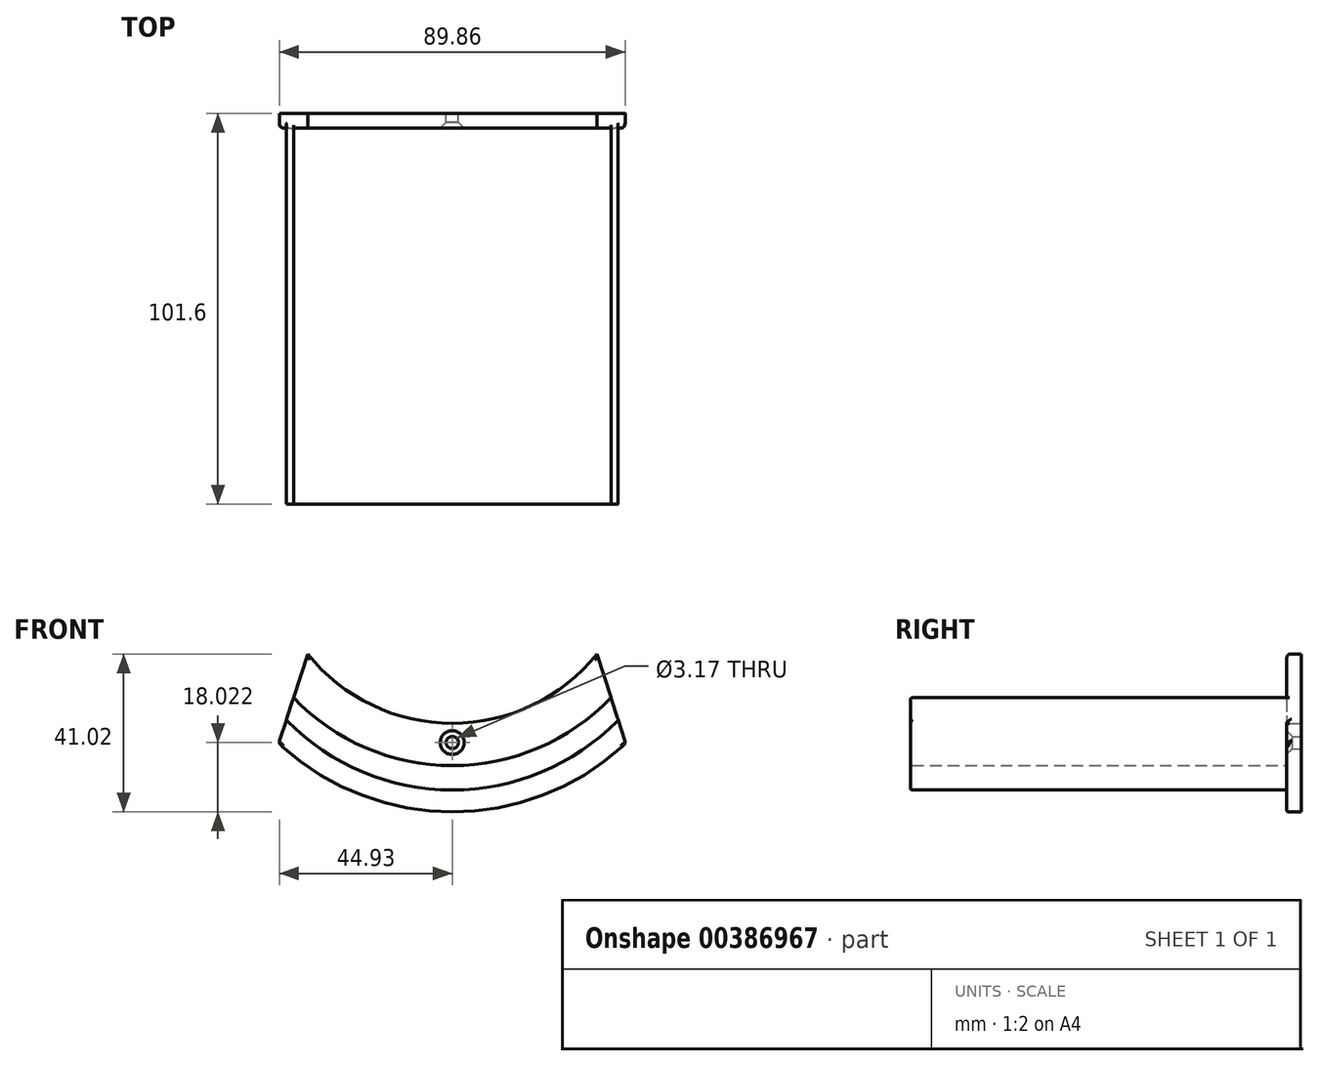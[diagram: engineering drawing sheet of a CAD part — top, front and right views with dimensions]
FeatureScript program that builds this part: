
annotation { "Feature Type Name" : "Feature", "Feature Type Description" : "" }
export const myFeature = defineFeature(function(context is Context, id is Id, definition is map)
    precondition{}
    {
        {
            var Q0;
            Q0=qCreatedBy(makeId("Front.planeOp"),FACE);
            var sketch = newSketch(context, id + "F0", { "sketchPlane" : qUnion([Q0])});
            skArc(sketch, "E0", {"start": v(-43.16, 1.57) * mm, "mid": v(0, -16.6) * mm, "end": v(43.16, 1.57) * mm});
            skArc(sketch, "E1", {"start": v(-41.28, 7.37) * mm, "mid": v(0, -10.26) * mm, "end": v(41.28, 7.37) * mm});
            skLineSegment(sketch, "E2", {"start": v(-43.16, 1.57) * mm, "end": v(-41.28, 7.37) * mm});
            skArc(sketch, "E3", {"start": v(-45.12, -4.47) * mm, "mid": v(0, -22.3) * mm, "end": v(45.12, -4.47) * mm});
            skLineSegment(sketch, "E4", {"start": v(-45.12, -4.47) * mm, "end": v(-43.16, 1.57) * mm});
            skLineSegment(sketch, "E5", {"start": v(45.12, -4.47) * mm, "end": v(43.16, 1.57) * mm});
            skPoint(sketch, "E6", {"position": v(0, -10.26) * mm});
            skPoint(sketch, "E7", {"position": v(0, -16.6) * mm});
            skLineSegment(sketch, "E8", {"start": v(43.16, 1.57) * mm, "end": v(41.28, 7.37) * mm});
            skCircle(sketch, "E9", {"center": v(0, -4.27) * mm, "radius": 1.59 * mm});
            skLineSegment(sketch, "E10", {"start": v(-41.28, 7.37) * mm, "end": v(-37.6, 18.73) * mm});
            skLineSegment(sketch, "E11", {"start": v(41.28, 7.37) * mm, "end": v(37.6, 18.73) * mm});
            skArc(sketch, "E12", {"start": v(-37.6, 18.73) * mm, "mid": v(0, 0.72) * mm, "end": v(37.6, 18.73) * mm});
            skSolve(sketch);
        }
        {
            var Q0;
            Q0=makeQuery(id+"F0.imprint","IMPRINT",FACE,{"disambiguationData":[TD([[makeQuery(id+"F0.imprint","IMPRINT",EDGE,{"derivedFrom":sQuery(id+"F0.wireOp",EDGE,"E0")}),1.0]])]});
            extrude(context, id + "F1", {"entities" : qUnion([Q0]), "depth" : 101.6 * mm, "offsetDistance" : 25.4 * mm});
        }
        {
            var Q0;
            Q0=makeQuery(id+"F0.imprint","IMPRINT",FACE,{"disambiguationData":[TD([[makeQuery(id+"F0.imprint","IMPRINT",EDGE,{"derivedFrom":sQuery(id+"F0.wireOp",EDGE,"E0")}),-1.0]])]});
            var Q1;
            {var subQ0=sQuery(id+"F0.wireOp",EDGE,"E5");Q1=makeQuery(id+"F0.imprint","IMPRINT",FACE,{"disambiguationData":[TD([[makeQuery(id+"F0.imprint","IMPRINT",EDGE,{"derivedFrom":subQ0}),1.0]])]});}
            var Q2;
            {var subQ0=sQuery(id+"F0.wireOp",EDGE,"E4");Q2=makeQuery(id+"F0.imprint","IMPRINT",FACE,{"disambiguationData":[TD([[makeQuery(id+"F0.imprint","IMPRINT",EDGE,{"derivedFrom":subQ0}),-1.0]])]});}
            extrude(context, id + "F2", {"entities" : qUnion([Q0, Q1, Q2]), "operationType" : NewBodyOperationType.ADD, "offsetDistance" : 25.4 * mm, "depth" : 3.8 * mm});
        }
        {
            var Q0;
            Q0=makeQuery(id+"F2.boolean.opBoolean","SPLIT",EDGE,{"derivedFrom":makeQuery(id+"F1.opExtrude","SWEPT_EDGE",EDGE,{"disambiguationData":[OSD([sQuery(id+"F0.wireOp",EDGE,"E0"),sQuery(id+"F0.wireOp",EDGE,"E5"),sQuery(id+"F0.wireOp",EDGE,"yFwQgnOm-BBmB-Px7s-qRVQ-lXTr3TJ4TYEj"),sQuery(id+"F0.wireOp",EDGE,"E8")])]})});
            var Q1;
            Q1=makeQuery(id+"F2.boolean.opBoolean","SPLIT",EDGE,{"derivedFrom":makeQuery(id+"F1.opExtrude","SWEPT_EDGE",EDGE,{"disambiguationData":[OSD([sQuery(id+"F0.wireOp",EDGE,"E0"),sQuery(id+"F0.wireOp",EDGE,"E2"),sQuery(id+"F0.wireOp",EDGE,"E4"),sQuery(id+"F0.wireOp",EDGE,"QKl4zN9S-gDWU-db6M-HyM4-Xh01oV9ZsjPb")])]})});
            var Q2;
            Q2=makeQuery(id+"F2.opExtrude","CAP_EDGE",EDGE,{"disambiguationData":[OSD([sQuery(id+"F0.wireOp",EDGE,"E3")])],"isStart":false});
            var Q3;
            Q3=makeQuery(id+"F1.opExtrude","CAP_EDGE",EDGE,{"disambiguationData":[OSD([sQuery(id+"F0.wireOp",EDGE,"E0")])],"isStart":false});
            var Q4;
            Q4=makeQuery(id+"F1.opExtrude","CAP_EDGE",EDGE,{"disambiguationData":[OSD([sQuery(id+"F0.wireOp",EDGE,"E1")])],"isStart":false});
            fillet(context, id + "F3", {"entities" : qUnion([Q0, Q1, Q2, Q3, Q4]), "radius" : 0.5 * mm, "defaultsChanged" : false, "vertexSettings" : [], "allowEdgeOverflow" : false});
        }
        {
            var Q0;
            Q0=makeQuery(id+"F2.opExtrude","CAP_EDGE",EDGE,{"disambiguationData":[OSD([sQuery(id+"F0.wireOp",EDGE,"E4")])],"isStart":false});
            var Q1;
            Q1=makeQuery(id+"F2.opExtrude","CAP_EDGE",EDGE,{"disambiguationData":[OSD([sQuery(id+"F0.wireOp",EDGE,"E5")])],"isStart":false});
            fillet(context, id + "F4", {"entities" : qUnion([Q0, Q1]), "radius" : 1.27 * mm, "tangentPropagation" : true, "allowEdgeOverflow" : false});
        }
        {
            var Q0;
            Q0=makeQuery(id+"F0.imprint","IMPRINT",FACE,{"disambiguationData":[TD([[makeQuery(id+"F0.imprint","IMPRINT",EDGE,{"derivedFrom":sQuery(id+"F0.wireOp",EDGE,"E9")}),-1.0]])]});
            extrude(context, id + "F5", {"entities" : qUnion([Q0]), "operationType" : NewBodyOperationType.ADD, "depth" : 3.8 * mm, "offsetDistance" : 25.4 * mm});
        }
        {
            var Q0;
            Q0=makeQuery(id+"F5.opExtrude","CAP_EDGE",EDGE,{"disambiguationData":[OSD([sQuery(id+"F0.wireOp",EDGE,"E9")])],"isStart":false});
            chamfer(context, id + "F6", {"entities" : qUnion([Q0]), "chamferType" : ChamferType.OFFSET_ANGLE, "width" : 1.52 * mm, "oppositeDirection" : false, "angle" : 45 * degree, "tangentPropagation" : true});
        }
        {
            var Q0;
            Q0=makeQuery(id+"F5.opExtrude","CAP_EDGE",EDGE,{"disambiguationData":[OSD([sQuery(id+"F0.wireOp",EDGE,"E12")])],"isStart":false});
            var Q1;
            Q1=makeQuery(id+"F5.opExtrude","CAP_EDGE",EDGE,{"disambiguationData":[OSD([sQuery(id+"F0.wireOp",EDGE,"E10")])],"isStart":false});
            var Q2;
            Q2=makeQuery(id+"F5.opExtrude","CAP_EDGE",EDGE,{"disambiguationData":[OSD([sQuery(id+"F0.wireOp",EDGE,"E11")])],"isStart":false});
            fillet(context, id + "F7", {"entities" : qUnion([Q0, Q1, Q2]), "tangentPropagation" : true, "radius" : 0.76 * mm, "defaultsChanged" : true, "vertexSettings" : [], "allowEdgeOverflow" : false});
        }
    });
